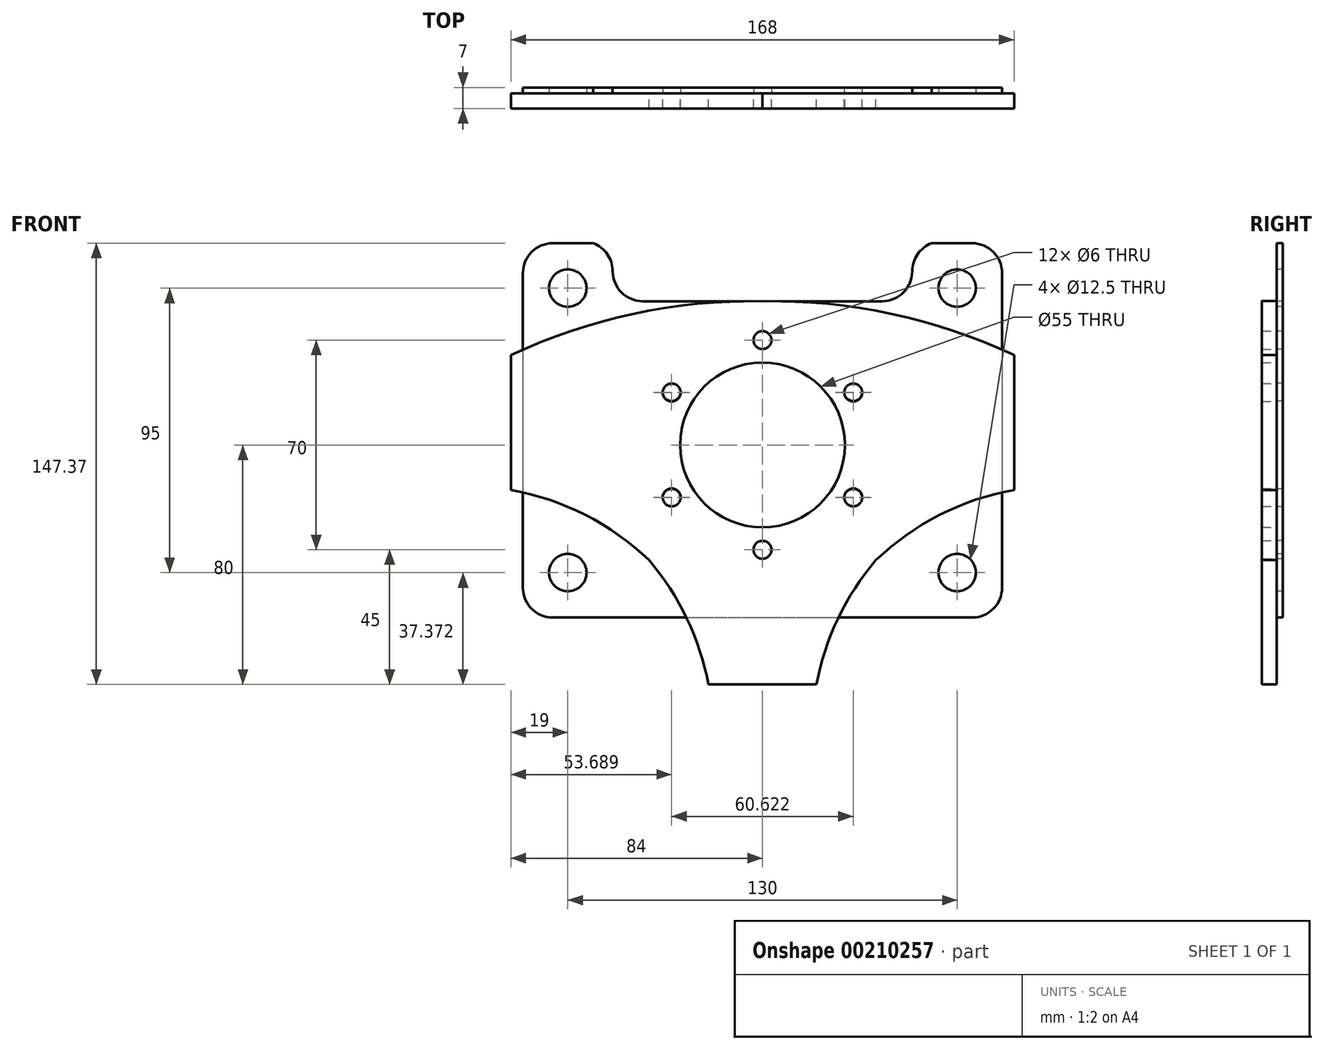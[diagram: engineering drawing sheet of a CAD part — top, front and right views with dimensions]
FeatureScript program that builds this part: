
annotation { "Feature Type Name" : "Feature", "Feature Type Description" : "" }
export const myFeature = defineFeature(function(context is Context, id is Id, definition is map)
    precondition{}
    {
        {
            var Q0;
            Q0=qCreatedBy(makeId("Front.planeOp"),FACE);
            var sketch = newSketch(context, id + "F0", { "sketchPlane" : qUnion([Q0])});
            skCircle(sketch, "E0", {"center": v(0, 0) * mm, "radius": 27.5 * mm});
            skCircle(sketch, "E1", {"center": v(0, 35) * mm, "radius": 3 * mm});
            skCircle(sketch, "E2.1.0", {"center": v(-30.31, 17.5) * mm, "radius": 3 * mm});
            skCircle(sketch, "E2.2.0", {"center": v(-30.31, -17.5) * mm, "radius": 3 * mm});
            skCircle(sketch, "E2.3.0", {"center": v(0, -35) * mm, "radius": 3 * mm});
            skCircle(sketch, "E2.4.0", {"center": v(30.31, -17.5) * mm, "radius": 3 * mm});
            skCircle(sketch, "E2.5.0", {"center": v(30.31, 17.5) * mm, "radius": 3 * mm});
            skLineSegment(sketch, "E3", {"start": v(0, -80) * mm, "end": v(-18, -80) * mm});
            skArc(sketch, "E4", {"start": v(-37.9, -38.47) * mm, "mid": v(-59.22, -23.35) * mm, "end": v(-84, -15) * mm});
            skArc(sketch, "E5", {"start": v(-18, -80) * mm, "mid": v(-25.25, -57.94) * mm, "end": v(-37.9, -38.47) * mm});
            skLineSegment(sketch, "E6", {"start": v(-84, 30) * mm, "end": v(-84, -15) * mm});
            skArc(sketch, "E7", {"start": v(0, 48) * mm, "mid": v(-43.03, 43.8) * mm, "end": v(-84, 30) * mm});
            skArc(sketch, "E8.MirrorCS", {"start": v(0, 48) * mm, "mid": v(43.03, 43.8) * mm, "end": v(84, 30) * mm});
            skLineSegment(sketch, "E9.MirrorCS", {"start": v(84, 30) * mm, "end": v(84, -15) * mm});
            skLineSegment(sketch, "E10.MirrorCS", {"start": v(84, -15) * mm, "end": v(84, -15) * mm});
            skArc(sketch, "E11.MirrorCS", {"start": v(37.9, -38.47) * mm, "mid": v(59.22, -23.35) * mm, "end": v(84, -15) * mm});
            skArc(sketch, "E12.MirrorCS", {"start": v(18, -80) * mm, "mid": v(25.25, -57.94) * mm, "end": v(37.9, -38.47) * mm});
            skLineSegment(sketch, "E13.MirrorCS", {"start": v(0, -80) * mm, "end": v(18, -80) * mm});
            skLineSegment(sketch, "E14", {"start": v(0, 0) * mm, "end": v(37.9, -38.47) * mm});
            skSolve(sketch);
        }
        {
            var Q0;
            Q0=makeQuery(id+"F0.imprint","IMPRINT",FACE,{"disambiguationData":[TD([[makeQuery(id+"F0.imprint","IMPRINT",EDGE,{"derivedFrom":sQuery(id+"F0.wireOp",EDGE,"xvLfkQ3F-fgjy-q9Nn-lcfM-oA4vtxVeLGYN")}),-1.0]])]});
            var Q1;
            {var subQ0=sQuery(id+"F0.wireOp",EDGE,"IXeQJo4f-0NGN-wymH-wL35-tD5XUzaEt9Ii");Q1=makeQuery(id+"F0.imprint","IMPRINT",FACE,{"disambiguationData":[TD([[makeQuery(id+"F0.imprint","IMPRINT",EDGE,{"derivedFrom":subQ0}),-1.0]])]});}
            var Q2;
            Q2=makeQuery(id+"F0.imprint","IMPRINT",FACE,{"disambiguationData":[TD([[makeQuery(id+"F0.imprint","IMPRINT",EDGE,{"derivedFrom":sQuery(id+"F0.wireOp",EDGE,"E0")}),-1.0]])]});
            var Q3;
            {var subQ0=sQuery(id+"F0.wireOp",EDGE,"U97vX6Bn-T6Nm-C19i-UCoZ-bPOguSU8hI4x");Q3=makeQuery(id+"F0.imprint","IMPRINT",FACE,{"disambiguationData":[TD([[makeQuery(id+"F0.imprint","IMPRINT",EDGE,{"derivedFrom":subQ0}),-1.0]])]});}
            var Q4;
            Q4=makeQuery(id+"F0.imprint","IMPRINT",FACE,{"disambiguationData":[TD([[makeQuery(id+"F0.imprint","IMPRINT",EDGE,{"derivedFrom":sQuery(id+"F0.wireOp",EDGE,"iTDH6eJd-3ZuL-mUN2-QFPx-3khqCnK7DwfM")}),-1.0]])]});
            var Q5;
            {var subQ0=sQuery(id+"F0.wireOp",EDGE,"LSPlpz0O-uzcR-zpDg-bx14-Tm5pNzSKurLG");Q5=makeQuery(id+"F0.imprint","IMPRINT",FACE,{"disambiguationData":[TD([[makeQuery(id+"F0.imprint","IMPRINT",EDGE,{"derivedFrom":subQ0}),-1.0]])]});}
            var Q6;
            Q6=makeQuery(id+"F0.imprint","IMPRINT",FACE,{"disambiguationData":[TD([[makeQuery(id+"F0.imprint","IMPRINT",EDGE,{"derivedFrom":sQuery(id+"F0.wireOp",EDGE,"9da5268f-547f-4821-a759-cff2299c6b0c0.MirrorC")}),1.0]])]});
            var Q7;
            Q7=makeQuery(id+"F0.imprint","IMPRINT",FACE,{"disambiguationData":[TD([[makeQuery(id+"F0.imprint","IMPRINT",EDGE,{"derivedFrom":sQuery(id+"F0.wireOp",EDGE,"5ea91802-01c1-4fcd-b629-e54decbf77210.MirrorC")}),1.0]])]});
            extrude(context, id + "F1", {"entities" : qUnion([Q0, Q1, Q2, Q3, Q4, Q5, Q6, Q7]), "depth" : 5 * mm});
        }
        {
            var Q0;
            Q0=qCreatedBy(makeId("Front.planeOp"),FACE);
            var sketch = newSketch(context, id + "F2", { "sketchPlane" : qUnion([Q0])});
            skLineSegment(sketch, "E15", {"start": v(-50, 57.83) * mm, "end": v(-50, 58) * mm});
            skLineSegment(sketch, "E16", {"start": v(-56.51, 67.37) * mm, "end": v(-56.51, 67.37) * mm});
            skPoint(sketch, "E17.visualSharp", {"position": v(-50, 64.95) * mm});
            skArc(sketch, "E17.filletArc", {"start": v(-50, 58) * mm, "mid": v(-51.79, 63.7) * mm, "end": v(-56.51, 67.37) * mm});
            skPoint(sketch, "E18.visualSharp", {"position": v(-50, 48) * mm});
            skLineSegment(sketch, "E19", {"start": v(0, 0) * mm, "end": v(0, 35) * mm});
            skCircle(sketch, "E20", {"center": v(-65, 52.37) * mm, "radius": 6.25 * mm});
            skPoint(sketch, "E21.center", {"position": v(0, 0) * mm});
            skCircle(sketch, "E22", {"center": v(-65, -42.63) * mm, "radius": 6.25 * mm});
            skLineSegment(sketch, "E23", {"start": v(-80, 57.37) * mm, "end": v(-80, -47.63) * mm});
            skLineSegment(sketch, "E24", {"start": v(-70, -57.63) * mm, "end": v(0, -57.63) * mm});
            skPoint(sketch, "E25.visualSharp", {"position": v(-80, -57.63) * mm});
            skArc(sketch, "E25.filletArc", {"start": v(-80, -47.63) * mm, "mid": v(-77.07, -54.7) * mm, "end": v(-70, -57.63) * mm});
            skLineSegment(sketch, "E26", {"start": v(-70, 67.37) * mm, "end": v(-56.51, 67.37) * mm});
            skPoint(sketch, "E27.visualSharp", {"position": v(-80, 67.37) * mm});
            skArc(sketch, "E27.filletArc", {"start": v(-70, 67.37) * mm, "mid": v(-77.07, 64.44) * mm, "end": v(-80, 57.37) * mm});
            skLineSegment(sketch, "E28", {"start": v(0, 35) * mm, "end": v(0, 48) * mm});
            skLineSegment(sketch, "E29", {"start": v(0, 48) * mm, "end": v(-40, 48) * mm});
            skLineSegment(sketch, "E30", {"start": v(-50, 58) * mm, "end": v(-50, 58) * mm});
            skArc(sketch, "E31.filletArc", {"start": v(-50, 58) * mm, "mid": v(-47.07, 50.93) * mm, "end": v(-40, 48) * mm});
            skCircle(sketch, "E32", {"center": v(-30.31, 17.64) * mm, "radius": 3 * mm});
            skCircle(sketch, "E33", {"center": v(0, 35) * mm, "radius": 3 * mm});
            skCircle(sketch, "E34.MirrorC", {"center": v(0, -35) * mm, "radius": 3 * mm});
            skCircle(sketch, "E35.MirrorC", {"center": v(-30.31, -17.64) * mm, "radius": 3 * mm});
            skCircle(sketch, "E36.MirrorC", {"center": v(30.31, 17.64) * mm, "radius": 3 * mm});
            skCircle(sketch, "E37.MirrorC", {"center": v(30.31, -17.64) * mm, "radius": 3 * mm});
            skLineSegment(sketch, "E38.MirrorCS", {"start": v(70, -57.63) * mm, "end": v(0, -57.63) * mm});
            skArc(sketch, "E39.MirrorCS", {"start": v(80, -47.63) * mm, "mid": v(77.07, -54.7) * mm, "end": v(70, -57.63) * mm});
            skLineSegment(sketch, "E40.MirrorCS", {"start": v(80, 57.37) * mm, "end": v(80, -47.63) * mm});
            skArc(sketch, "E41.MirrorCS", {"start": v(70, 67.37) * mm, "mid": v(77.07, 64.44) * mm, "end": v(80, 57.37) * mm});
            skArc(sketch, "E42.MirrorCS", {"start": v(50, 58) * mm, "mid": v(47.07, 50.93) * mm, "end": v(40, 48) * mm});
            skLineSegment(sketch, "E43.MirrorCS", {"start": v(0, 48) * mm, "end": v(40, 48) * mm});
            skArc(sketch, "E44.MirrorCS", {"start": v(50, 58) * mm, "mid": v(51.79, 63.7) * mm, "end": v(56.51, 67.37) * mm});
            skLineSegment(sketch, "E45.MirrorCS", {"start": v(70, 67.37) * mm, "end": v(56.51, 67.37) * mm});
            skCircle(sketch, "E46.MirrorC", {"center": v(65, 52.37) * mm, "radius": 6.25 * mm});
            skCircle(sketch, "E47.MirrorC", {"center": v(65, -42.63) * mm, "radius": 6.25 * mm});
            skSolve(sketch);
        }
        {
            var Q0;
            Q0=makeQuery(id+"F2.imprint","IMPRINT",FACE,{"disambiguationData":[TD([[makeQuery(id+"F2.imprint","IMPRINT",EDGE,{"derivedFrom":sQuery(id+"F2.wireOp",EDGE,"E17.filletArc")}),1.0]])]});
            extrude(context, id + "F3", {"entities" : qUnion([Q0]), "oppositeDirection" : true, "depth" : 2 * mm});
        }
    });
